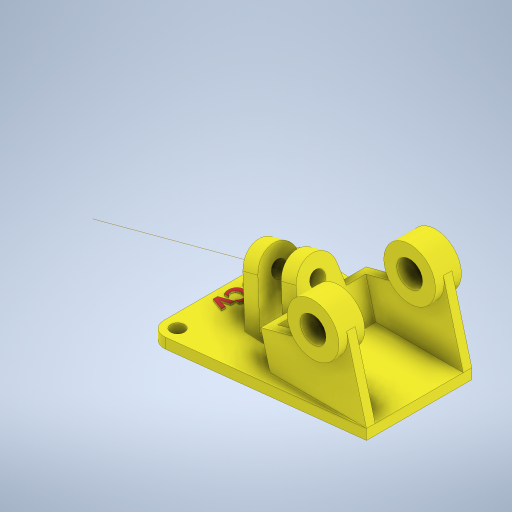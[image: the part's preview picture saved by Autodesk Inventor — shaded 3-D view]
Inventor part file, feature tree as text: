
AUTODESK INVENTOR PART (.ipt)
format: ipt  version: 2024 (Build 280153000, 153)  size: 487,936 bytes
history: native  units: mm
features: sketch x12, extrude x7, hole x4, other x2, emboss x1
ambient origin geometry x8: Origin, YZ Plane, XZ Plane, XY Plane, X Axis, Y Axis, Z Axis, Center Point
bodies: Solid1 (feature_tree)
feature tree (26):
  other  "Work Axis1"
  extrude  "Extrusion1"  Depth=9.0mm
  extrude  "Extrusion2"  Depth=117.0mm
  extrude  "Extrusion5"  Depth=35.0mm
  extrude  "Extrusion6"  Depth=12.0mm
  extrude  "Extrusion7"  Depth=13.613568mm
  extrude  "Extrusion8"  Depth=50.0mm TaperAngle=0.0deg
  extrude  "Extrusion9"  Depth=20.0mm
  hole  "Hole1"  [1 undecoded]
  hole  "Hole2"  [1 undecoded]
  hole  "Hole3"  [1 undecoded]
  hole  "Hole4"  [1 undecoded]
  emboss  "Emboss1"
  other  "Work Point1"
  sketch  "Sketch1"  dims[d0=9.0mm d1=9.0mm]
  sketch  "Sketch2"  dims[d2=12.0mm d3=117.0mm]
  sketch  "Sketch5"  dims[d4=14.0mm d5=35.0mm]
  sketch  "Sketch6"  dims[d6=50.0mm d7=0.0mm d8=12.0mm]
  sketch  "Sketch7"  dims[d9=13.613568mm d10=13.613568mm]
  sketch  "Sketch8"  dims[d11=15.0mm d12=50.0mm d13=0.0mm]
  sketch  "Sketch9"  dims[d23=5.0mm d24=20.0mm]
  sketch  "Sketch10"  dims[d25=30.0mm d26=49.0mm]
  sketch  "Sketch11"  dims[d27=61.0mm d28=0.0mm d29=5.0mm]
  sketch  "Sketch12"  dims[d30=5.0mm d31=5.0mm]
  sketch  "Sketch13"  dims[d32=5.0mm d33=61.0mm d34=0.0mm]
  sketch  "Sketch14"  dims[d35=30.0mm d36=71.0mm d37=0.0mm d38=39.0mm d39=41.0mm d40=0.0mm d41=8.0mm d42=113.0mm d43=70.0mm d44=35.0mm d45=6.0mm d46=0.0mm d47=15.0mm d48=6.0mm d49=4.0mm d50=2.0mm d51=90.0deg d52=8.0mm d53=20.594885mm d54=9.0mm d55=6.0mm d56=4.0mm d57=2.0mm d58=90.0deg d59=8.0mm d60=20.594885mm d61=8.0mm d62=6.0mm d63=4.0mm d64=2.0mm d65=90.0deg d66=8.0mm d67=20.594885mm d68=8.0mm d69=6.0mm d70=4.0mm d71=2.0mm d72=90.0deg d73=8.0mm d74=20.594885mm d75=15.0mm d76=29.0mm d77=11.0mm d78=1.0mm d79=0.0mm d21=0.5mm d22=0.872665mm]
note: 4 required parameter values undecoded (feature->parameter linkage not recoverable at this tier; creation-order binding heuristic only, values carry confidence <= 0.55)
